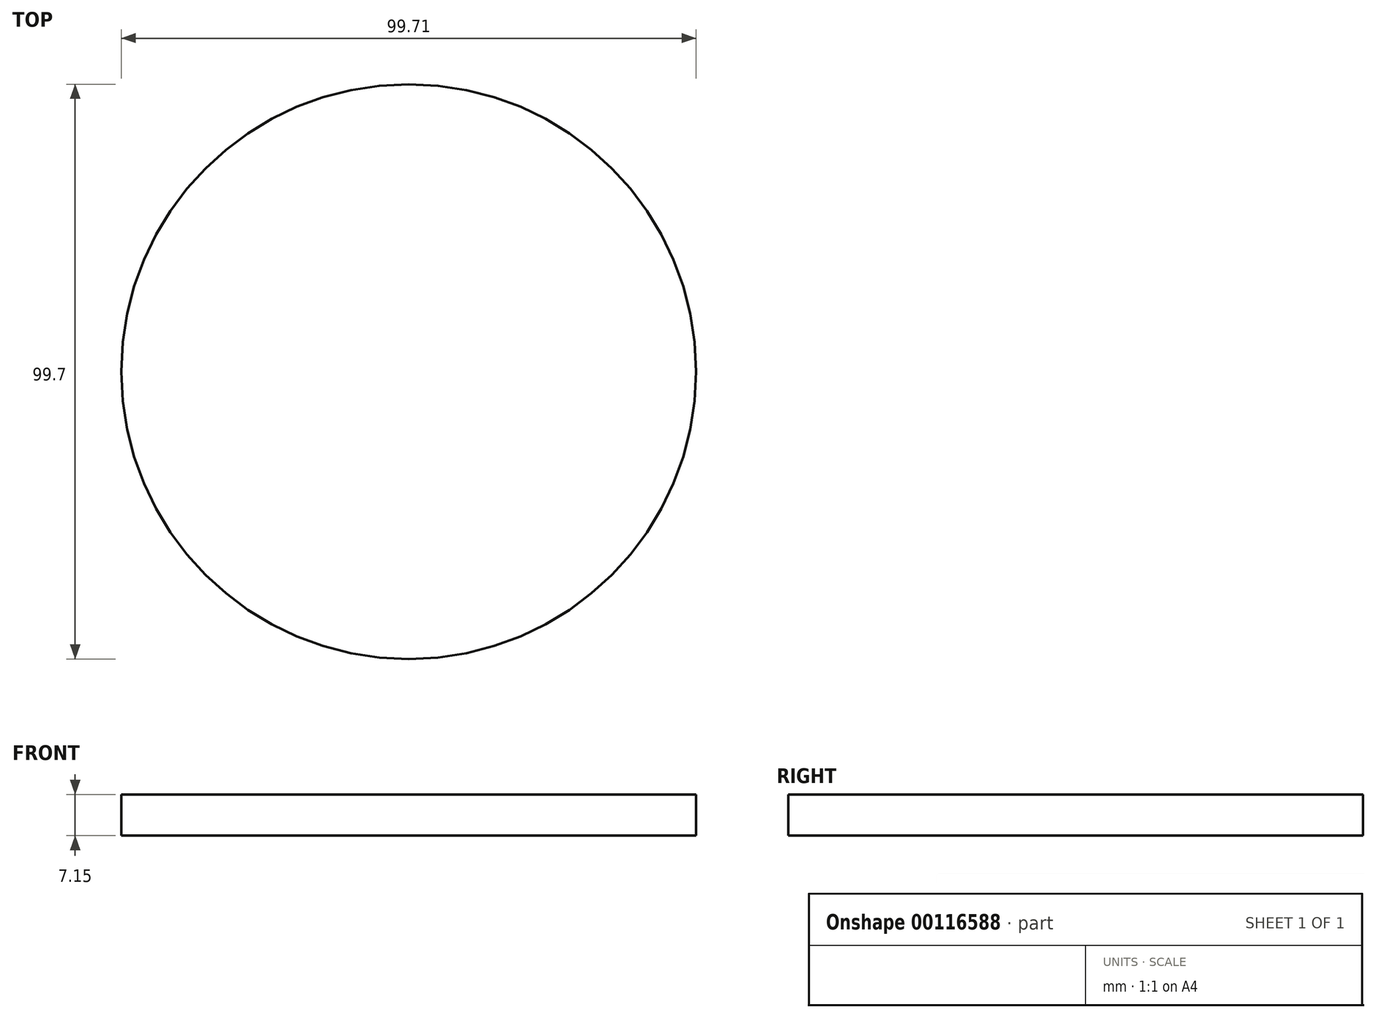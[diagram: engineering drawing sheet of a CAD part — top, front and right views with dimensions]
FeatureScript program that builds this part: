
annotation { "Feature Type Name" : "Feature", "Feature Type Description" : "" }
export const myFeature = defineFeature(function(context is Context, id is Id, definition is map)
    precondition{}
    {
        {
            var Q0;
            Q0=qCreatedBy(makeId("Front.planeOp"),FACE);
            var sketch = newSketch(context, id + "F0", { "sketchPlane" : qUnion([Q0])});
            skLineSegment(sketch, "E0.bottom", {"start": v(-25.39, 7.15) * mm, "end": v(24.46, 7.15) * mm});
            skLineSegment(sketch, "E0.top", {"start": v(-25.39, 0) * mm, "end": v(24.46, 0) * mm});
            skLineSegment(sketch, "E0.left", {"start": v(-25.39, 7.15) * mm, "end": v(-25.39, 0) * mm});
            skLineSegment(sketch, "E0.right", {"start": v(24.46, 7.15) * mm, "end": v(24.46, 0) * mm});
            skSolve(sketch);
        }
        {
            var Q0;
            Q0=makeQuery(id+"F0.imprint","IMPRINT",FACE,{"disambiguationData":[TD([[makeQuery(id+"F0.imprint","IMPRINT",EDGE,{"derivedFrom":sQuery(id+"F0.wireOp",EDGE,"E0.bottom")}),-1.0]])]});
            var Q1;
            Q1=sQuery(id+"F0.wireOp",EDGE,"E0.right");
            revolve(context, id + "F1", {"entities" : qUnion([Q0]), "axis" : qUnion([Q1]), "revolveType" : RevolveType.FULL});
        }
    });
